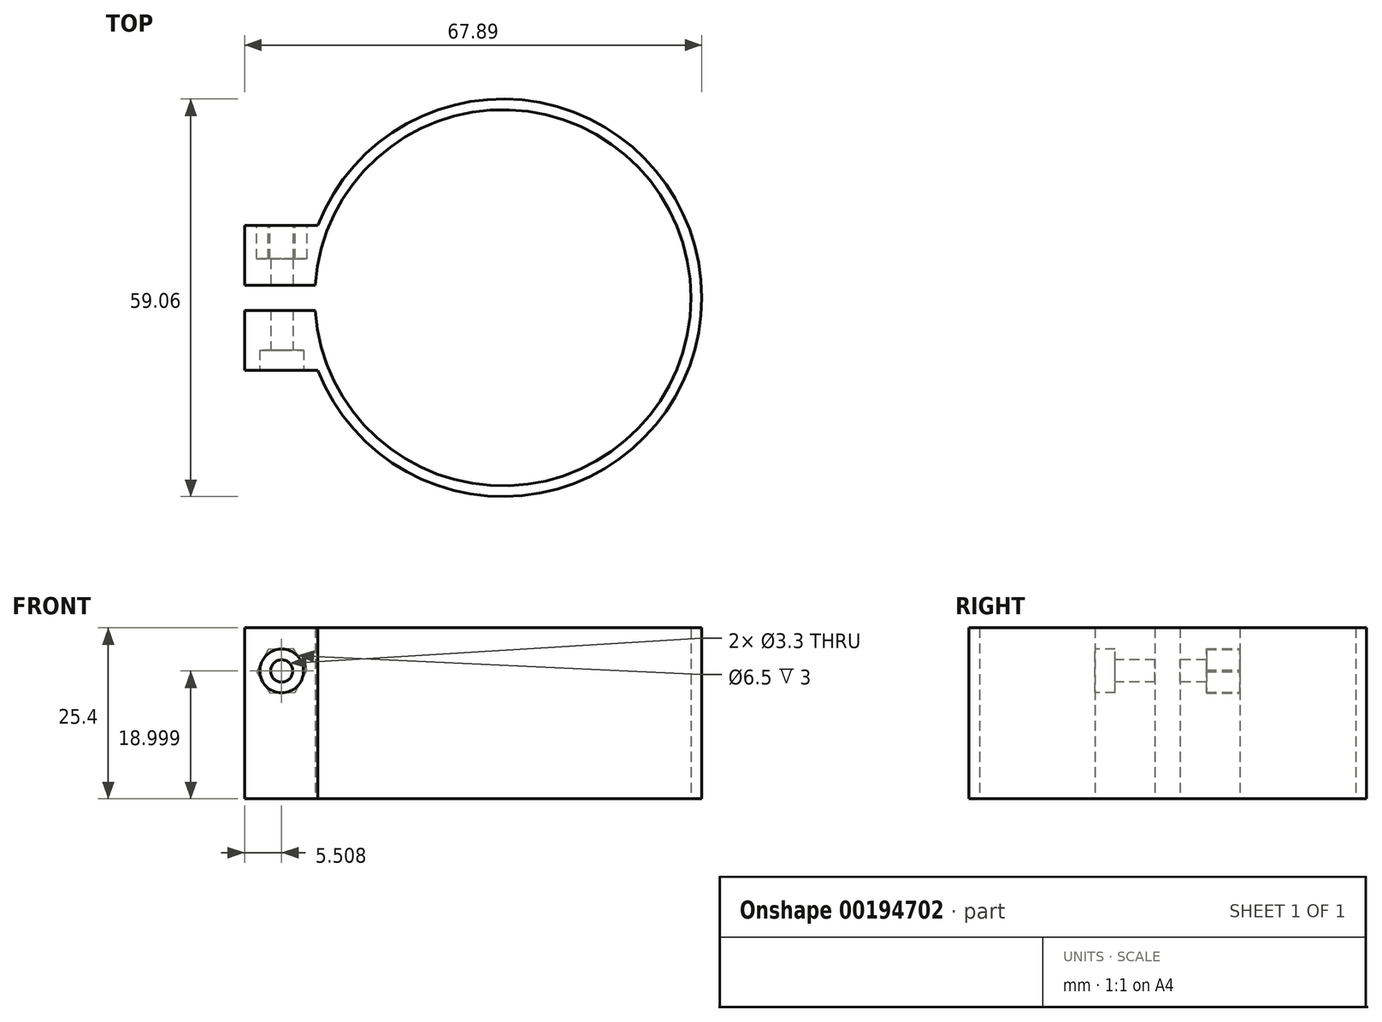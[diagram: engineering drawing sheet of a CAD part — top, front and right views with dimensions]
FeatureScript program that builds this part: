
annotation { "Feature Type Name" : "Feature", "Feature Type Description" : "" }
export const myFeature = defineFeature(function(context is Context, id is Id, definition is map)
    precondition{}
    {
        {
            var Q0;
            Q0=qCreatedBy(makeId("Top.planeOp"),FACE);
            var sketch = newSketch(context, id + "F0", { "sketchPlane" : qUnion([Q0])});
            skArc(sketch, "E0", {"start": v(-27.88, -1.88) * mm, "mid": v(27.94, 0) * mm, "end": v(-27.88, 1.88) * mm});
            skArc(sketch, "E1.0", {"start": v(-27.5, -10.77) * mm, "mid": v(29.53, 0) * mm, "end": v(-27.5, 10.77) * mm});
            skLineSegment(sketch, "E2.bottom", {"start": v(-27.88, -1.88) * mm, "end": v(-29.47, -1.88) * mm});
            skLineSegment(sketch, "E2.top", {"start": v(-27.88, 1.88) * mm, "end": v(-29.47, 1.88) * mm});
            skLineSegment(sketch, "E3.bottom", {"start": v(-29.47, 1.88) * mm, "end": v(-38.36, 1.88) * mm});
            skLineSegment(sketch, "E3.top", {"start": v(-29.47, 10.77) * mm, "end": v(-38.36, 10.77) * mm});
            skLineSegment(sketch, "E3.right", {"start": v(-38.36, 1.88) * mm, "end": v(-38.36, 10.77) * mm});
            skLineSegment(sketch, "E4.bottom", {"start": v(-29.47, -1.88) * mm, "end": v(-38.36, -1.88) * mm});
            skLineSegment(sketch, "E4.top", {"start": v(-29.47, -10.77) * mm, "end": v(-38.36, -10.77) * mm});
            skLineSegment(sketch, "E4.right", {"start": v(-38.36, -1.88) * mm, "end": v(-38.36, -10.77) * mm});
            skLineSegment(sketch, "E5", {"start": v(-29.47, 10.77) * mm, "end": v(-27.5, 10.77) * mm});
            skLineSegment(sketch, "E6", {"start": v(-29.47, -10.77) * mm, "end": v(-27.5, -10.77) * mm});
            skSolve(sketch);
        }
        {
            var Q0;
            Q0=makeQuery(id+"F0.imprint","IMPRINT",FACE,{"disambiguationData":[TD([[makeQuery(id+"F0.imprint","IMPRINT",EDGE,{"derivedFrom":sQuery(id+"F0.wireOp",EDGE,"E0")}),-1.0]])]});
            extrude(context, id + "F1", {"entities" : qUnion([Q0]), "depth" : 25.4 * mm});
        }
        {
            var Q0;
            Q0=makeQuery(id+"F1.opExtrude","SWEPT_FACE",FACE,{"disambiguationData":[OSD([sQuery(id+"F0.wireOp",EDGE,"E4.top"),sQuery(id+"F0.wireOp",EDGE,"E6")])]});
            var sketch = newSketch(context, id + "F2", { "sketchPlane" : qUnion([Q0])});
            skLineSegment(sketch, "E7", {"start": v(-32.93, 25.4) * mm, "end": v(-32.93, 0) * mm});
            skPoint(sketch, "E8", {"position": v(-32.85, 19) * mm});
            skSolve(sketch);
        }
        {
            var Q0;
            Q0=sQuery(id+"F2.wireOp",VERTEX,"E8");
            var Q1;
            Q1=makeQuery(id+"F1.opExtrude","SWEPT_BODY",BODY,{"disambiguationData":[OSD([sQuery(id+"F0.wireOp",EDGE,"E0"),sQuery(id+"F0.wireOp",EDGE,"E1.0"),sQuery(id+"F0.wireOp",EDGE,"E2.bottom"),sQuery(id+"F0.wireOp",EDGE,"E2.top"),sQuery(id+"F0.wireOp",EDGE,"E3.bottom"),sQuery(id+"F0.wireOp",EDGE,"E3.top"),sQuery(id+"F0.wireOp",EDGE,"E3.right"),sQuery(id+"F0.wireOp",EDGE,"E4.bottom"),sQuery(id+"F0.wireOp",EDGE,"E4.top"),sQuery(id+"F0.wireOp",EDGE,"E4.right"),sQuery(id+"F0.wireOp",EDGE,"E5"),sQuery(id+"F0.wireOp",EDGE,"E6")])]});
            hole(context, id + "F3", {"style" : HoleStyle.C_BORE, "endStyle" : HoleEndStyle.THROUGH, "standardTappedOrClearance" : lookupTablePath({ "standard" : "ISO", "fit" : "Normal", "size" : "M3", "type" : "Clearance" }), "standardBlindInLast" : lookupTablePath({ "fit" : "Standard", "standard" : "ISO", "size" : "M3", "type" : "Clearance" }), "holeDiameter" : 3.3 * mm, "cBoreDiameter" : 6.5 * mm, "cBoreDepth" : 3 * mm, "locations" : qUnion([Q0]), "scope" : qUnion([Q1]), "isTappedThrough" : true});
        }
        {
            var Q0;
            Q0=makeQuery(id+"F1.opExtrude","SWEPT_FACE",FACE,{"disambiguationData":[OSD([sQuery(id+"F0.wireOp",EDGE,"E3.top"),sQuery(id+"F0.wireOp",EDGE,"E5")])]});
            var sketch = newSketch(context, id + "F4", { "sketchPlane" : qUnion([Q0])});
            skCircle(sketch, "E9.cCircle", {"center": v(32.85, 19) * mm, "radius": 3.25 * mm, "construction": true});
            skLineSegment(sketch, "E9.0", {"start": v(36.6, 18.86) * mm, "end": v(34.6, 15.69) * mm});
            skLineSegment(sketch, "E9.1", {"start": v(34.6, 15.69) * mm, "end": v(30.86, 15.82) * mm});
            skLineSegment(sketch, "E9.2", {"start": v(30.86, 15.82) * mm, "end": v(29.1, 19.13) * mm});
            skLineSegment(sketch, "E9.3", {"start": v(29.1, 19.13) * mm, "end": v(31.1, 22.31) * mm});
            skLineSegment(sketch, "E9.4", {"start": v(31.1, 22.31) * mm, "end": v(34.84, 22.18) * mm});
            skLineSegment(sketch, "E9.5", {"start": v(34.84, 22.18) * mm, "end": v(36.6, 18.86) * mm});
            skPoint(sketch, "E9.0.midPoint", {"position": v(35.6, 17.27) * mm});
            skSolve(sketch);
        }
        {
            var Q0;
            Q0 = qSketchRegion(id + "F4", true);
            extrude(context, id + "F5", {"entities" : qUnion([Q0]), "operationType" : NewBodyOperationType.REMOVE, "oppositeDirection" : true, "depth" : 5 * mm});
        }
    });
